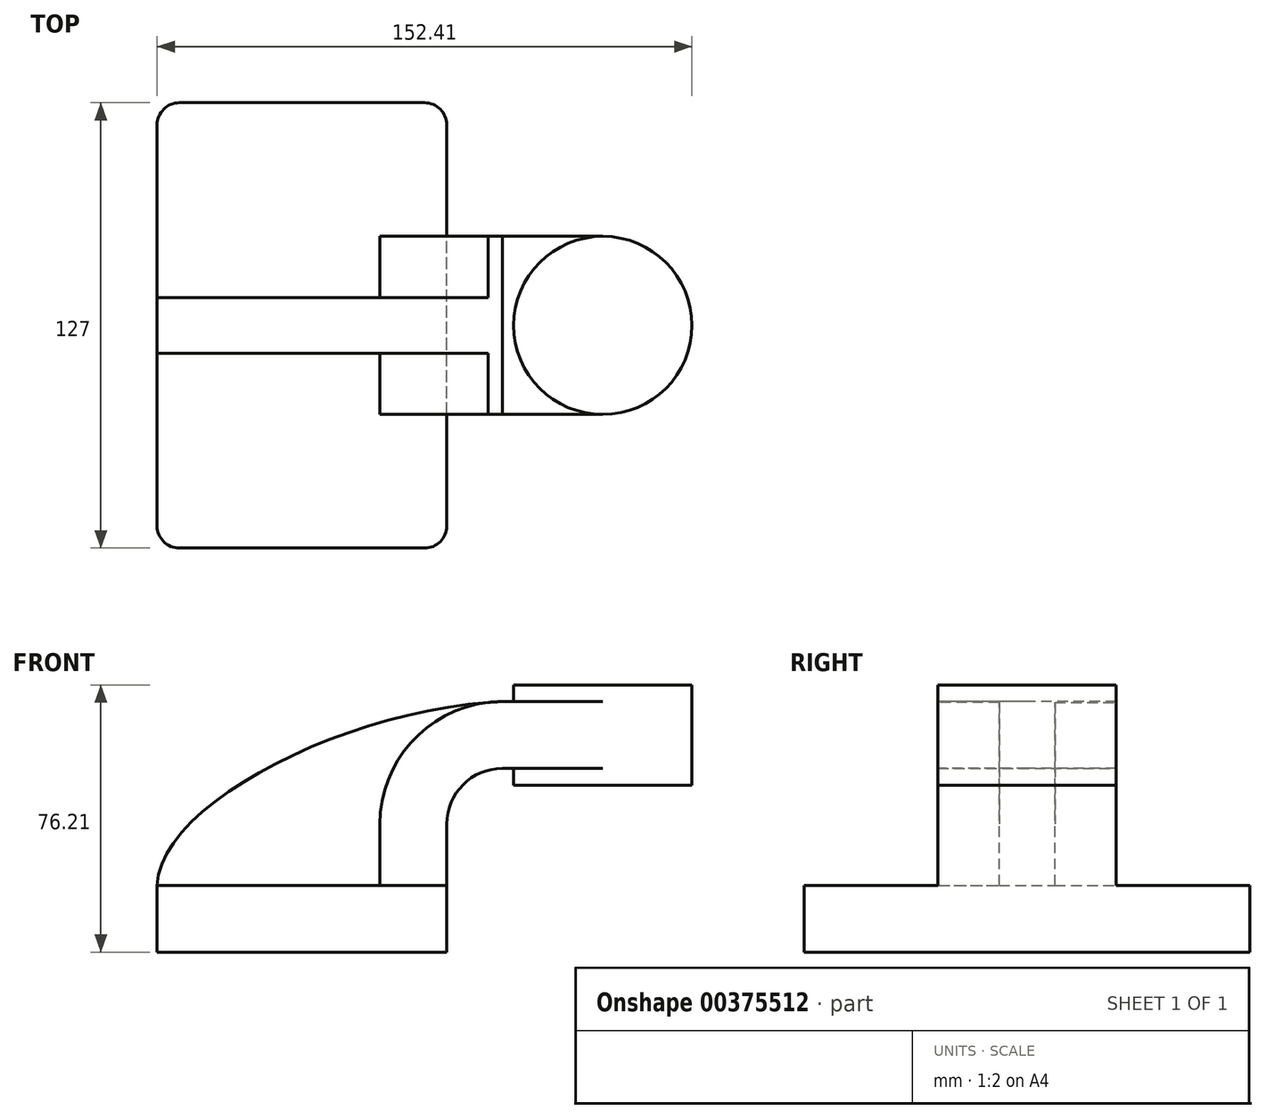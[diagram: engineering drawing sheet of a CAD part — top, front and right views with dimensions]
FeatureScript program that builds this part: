
annotation { "Feature Type Name" : "Feature", "Feature Type Description" : "" }
export const myFeature = defineFeature(function(context is Context, id is Id, definition is map)
    precondition{}
    {
        {
            var Q0;
            Q0=qCreatedBy(makeId("Front.planeOp"),FACE);
            var sketch = newSketch(context, id + "F0", { "sketchPlane" : qUnion([Q0])});
            skLineSegment(sketch, "E0.bottom", {"start": v(41.27, 9.53) * mm, "end": v(-41.27, 9.53) * mm});
            skLineSegment(sketch, "E0.top", {"start": v(41.28, -9.52) * mm, "end": v(-41.27, -9.52) * mm});
            skLineSegment(sketch, "E0.left", {"start": v(41.28, 9.53) * mm, "end": v(41.28, -9.52) * mm});
            skLineSegment(sketch, "E0.right", {"start": v(-41.27, 9.53) * mm, "end": v(-41.27, -9.52) * mm});
            skPoint(sketch, "E0.middle", {"position": v(0, 0) * mm});
            skLineSegment(sketch, "E1.bottom", {"start": v(60.33, 38.1) * mm, "end": v(111.13, 38.1) * mm});
            skLineSegment(sketch, "E1.top", {"start": v(60.33, 66.68) * mm, "end": v(111.13, 66.68) * mm});
            skLineSegment(sketch, "E1.left", {"start": v(60.33, 38.1) * mm, "end": v(60.33, 66.68) * mm});
            skLineSegment(sketch, "E1.right", {"start": v(111.13, 38.1) * mm, "end": v(111.13, 66.68) * mm});
            skPoint(sketch, "E1.middle", {"position": v(85.73, 52.39) * mm});
            skLineSegment(sketch, "E2", {"start": v(41.27, 9.53) * mm, "end": v(41.27, 27) * mm});
            skArc(sketch, "E3", {"start": v(41.27, 27) * mm, "mid": v(45.9, 38.2) * mm, "end": v(57.08, 42.88) * mm});
            skFitSpline(sketch, "E4", {"points": [v(-41.28, 9.53) * mm, v(57.15, 61.93) * mm], "startDerivative": vector(2.62, 70.63) * mm, "endDerivative": vector(131.4, 5.55) * mm});
            skLineSegment(sketch, "E5", {"start": v(57.08, 42.88) * mm, "end": v(85.73, 42.88) * mm});
            skPoint(sketch, "E5.endSnap0", {"position": v(85.73, 38.1) * mm});
            skLineSegment(sketch, "E6.0", {"start": v(57.04, 61.93) * mm, "end": v(85.73, 61.93) * mm});
            skArc(sketch, "E6.1", {"start": v(22.22, 27) * mm, "mid": v(32.42, 51.66) * mm, "end": v(57.04, 61.93) * mm});
            skLineSegment(sketch, "E6.2", {"start": v(22.22, 9.53) * mm, "end": v(22.22, 27) * mm});
            skLineSegment(sketch, "E7", {"start": v(85.73, 38.1) * mm, "end": v(85.73, 66.68) * mm});
            skSolve(sketch);
        }
        {
            var Q0;
            Q0=makeQuery(id+"F0.imprint","IMPRINT",FACE,{"disambiguationData":[TD([[makeQuery(id+"F0.imprint","IMPRINT",EDGE,{"derivedFrom":sQuery(id+"F0.wireOp",EDGE,"E0.top")}),-1.0]])]});
            extrude(context, id + "F1", {"entities" : qUnion([Q0]), "endBound" : BoundingType.SYMMETRIC, "depth" : 127 * mm});
        }
        {
            var Q0;
            {var subQ1=sQuery(id+"F0.wireOp",EDGE,"E2");Q0=makeQuery(id+"F0.imprint","IMPRINT",FACE,{"disambiguationData":[TD([[makeQuery(id+"F0.imprint","IMPRINT",EDGE,{"derivedFrom":subQ1}),1.0]])]});}
            var Q1;
            {var subQ5=sQuery(id+"F0.wireOp",EDGE,"o1RdE3cy-HKRY-kh1O-01tM-PWjN9G9jCkjA");Q1=makeQuery(id+"F0.imprint","IMPRINT",FACE,{"disambiguationData":[TD([[makeQuery(id+"F0.imprint","IMPRINT",EDGE,{"derivedFrom":subQ5}),-1.0]])]});}
            var Q2;
            {var subQ0=sQuery(id+"F0.wireOp",EDGE,"E5");var subQ1=sQuery(id+"F0.wireOp",EDGE,"E1.left");var subQ2=makeQuery(id+"F0.imprint","INTERSECT",VERTEX,{"derivedFrom":[subQ1,subQ0]});Q2=makeQuery(id+"F0.imprint","IMPRINT",FACE,{"disambiguationData":[TD([[makeQuery(id+"F0.imprint","IMPRINT",EDGE,{"disambiguationData":[TD([[subQ2,-1.0]])],"derivedFrom":subQ1}),-1.0]])]});}
            extrude(context, id + "F2", {"entities" : qUnion([Q0, Q1, Q2]), "operationType" : NewBodyOperationType.ADD, "endBound" : BoundingType.SYMMETRIC, "depth" : 50.8 * mm});
        }
        {
            var Q0;
            {var subQ3=sQuery(id+"F0.wireOp",EDGE,"E6.2");Q0=makeQuery(id+"F0.imprint","IMPRINT",FACE,{"disambiguationData":[TD([[makeQuery(id+"F0.imprint","IMPRINT",EDGE,{"derivedFrom":subQ3}),1.0]])]});}
            extrude(context, id + "F3", {"entities" : qUnion([Q0]), "operationType" : NewBodyOperationType.ADD, "endBound" : BoundingType.SYMMETRIC, "depth" : 15.88 * mm});
        }
        {
            var Q0;
            {var subQ4=sQuery(id+"F0.wireOp",EDGE,"E1.right");Q0=makeQuery(id+"F0.imprint","IMPRINT",FACE,{"disambiguationData":[TD([[makeQuery(id+"F0.imprint","IMPRINT",EDGE,{"derivedFrom":subQ4}),1.0]])]});}
            var Q1;
            Q1=sQuery(id+"F0.wireOp",EDGE,"E7");
            revolve(context, id + "F4", {"operationType" : NewBodyOperationType.ADD, "entities" : qUnion([Q0]), "axis" : qUnion([Q1]), "revolveType" : RevolveType.FULL});
        }
        {
            var Q0;
            Q0=makeQuery(id+"F1.opExtrude","CAP_EDGE",EDGE,{"disambiguationData":[OSD([sQuery(id+"F0.wireOp",EDGE,"E0.left")])],"isStart":false});
            var Q1;
            Q1=makeQuery(id+"F1.opExtrude","CAP_EDGE",EDGE,{"disambiguationData":[OSD([sQuery(id+"F0.wireOp",EDGE,"E0.right")])],"isStart":false});
            var Q2;
            Q2=makeQuery(id+"F1.opExtrude","CAP_EDGE",EDGE,{"disambiguationData":[OSD([sQuery(id+"F0.wireOp",EDGE,"E0.left")])],"isStart":true});
            var Q3;
            Q3=makeQuery(id+"F1.opExtrude","CAP_EDGE",EDGE,{"disambiguationData":[OSD([sQuery(id+"F0.wireOp",EDGE,"E0.right")])],"isStart":true});
            fillet(context, id + "F5", {"entities" : qUnion([Q0, Q1, Q2, Q3]), "radius" : 6.35 * mm, "tangentPropagation" : true, "allowEdgeOverflow" : false});
        }
    });
